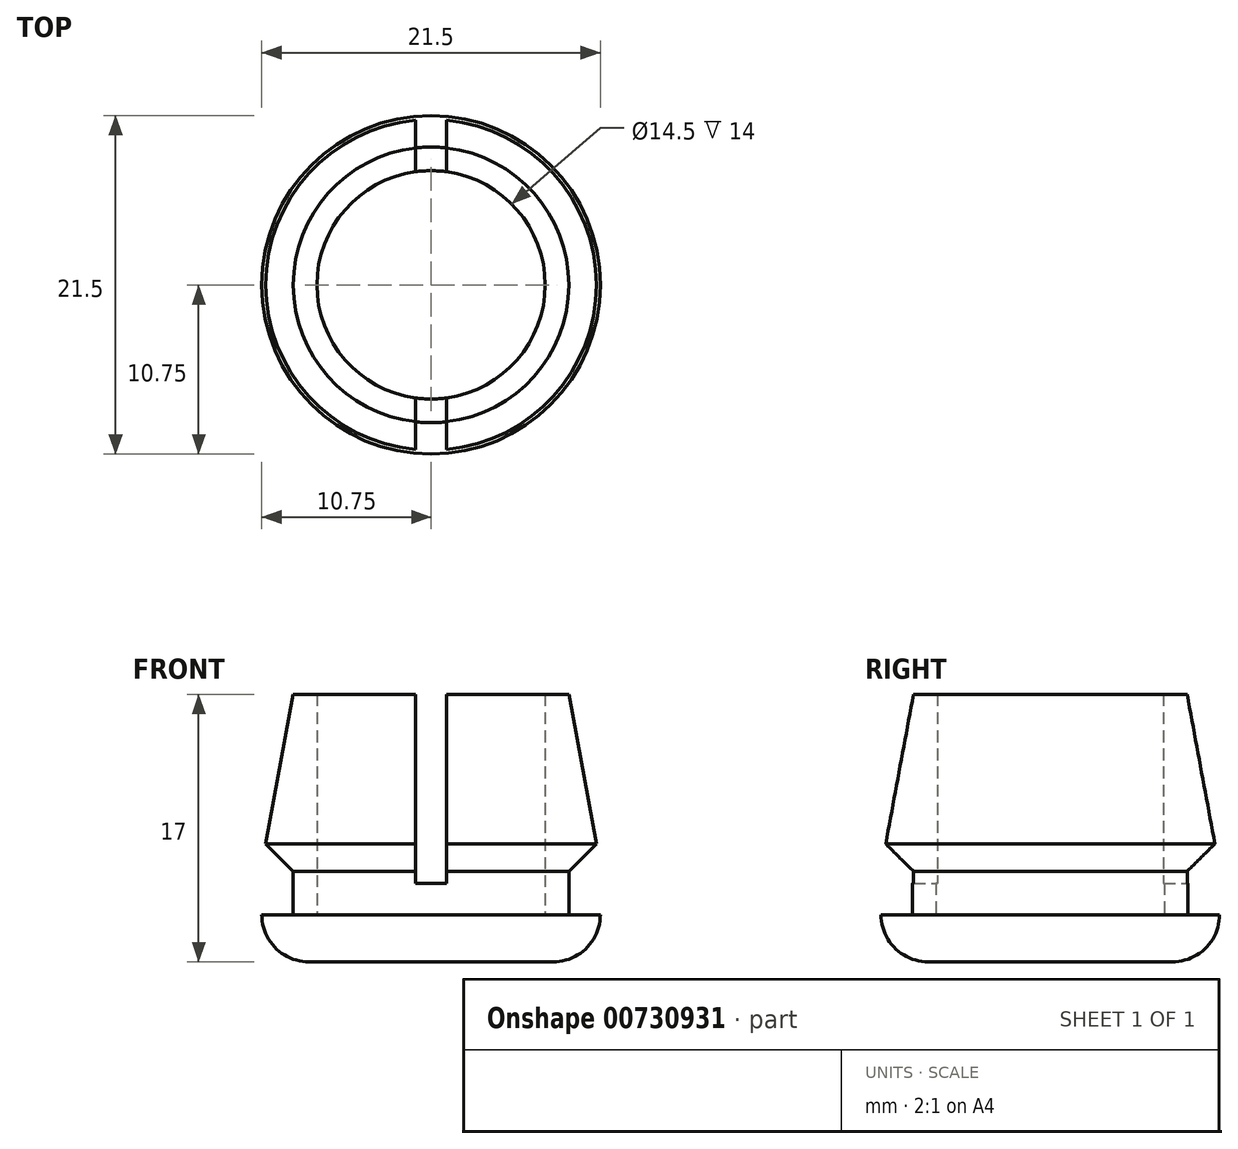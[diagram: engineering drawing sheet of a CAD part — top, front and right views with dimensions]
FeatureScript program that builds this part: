
annotation { "Feature Type Name" : "Feature", "Feature Type Description" : "" }
export const myFeature = defineFeature(function(context is Context, id is Id, definition is map)
    precondition{}
    {
        {
            var Q0;
            Q0=qCreatedBy(makeId("Front.planeOp"),FACE);
            var sketch = newSketch(context, id + "F0", { "sketchPlane" : qUnion([Q0])});
            skLineSegment(sketch, "E0", {"start": v(0, 0) * mm, "end": v(10.75, 0) * mm});
            skLineSegment(sketch, "E1", {"start": v(10.75, 0) * mm, "end": v(10.75, 3) * mm});
            skLineSegment(sketch, "E2", {"start": v(10.75, 3) * mm, "end": v(8.75, 3) * mm});
            skLineSegment(sketch, "E3", {"start": v(8.75, 3) * mm, "end": v(8.75, 7.5) * mm});
            skLineSegment(sketch, "E4", {"start": v(8.75, 7.5) * mm, "end": v(10.5, 7.5) * mm});
            skLineSegment(sketch, "E5", {"start": v(10.5, 7.5) * mm, "end": v(8.75, 17) * mm});
            skLineSegment(sketch, "E6", {"start": v(8.75, 17) * mm, "end": v(7.25, 17) * mm});
            skLineSegment(sketch, "E7", {"start": v(7.25, 17) * mm, "end": v(7.25, 3) * mm});
            skLineSegment(sketch, "E8", {"start": v(7.25, 3) * mm, "end": v(0, 3) * mm});
            skLineSegment(sketch, "E9", {"start": v(0, 0) * mm, "end": v(0, 3) * mm});
            skSolve(sketch);
        }
        {
            var Q0;
            Q0=makeQuery(id+"F0.imprint","IMPRINT",FACE,{"disambiguationData":[TD([[makeQuery(id+"F0.imprint","IMPRINT",EDGE,{"derivedFrom":sQuery(id+"F0.wireOp",EDGE,"E0")}),1.0]])]});
            var Q1;
            Q1 = qConstructionFilter(qBodyType(qCreatedBy(id + "F0" ,EDGE), BodyType.WIRE), ConstructionObject.NO);
            var Q2;
            Q2=sQuery(id+"F0.wireOp",EDGE,"E9");
            revolve(context, id + "F1", {"surfaceOperationType" : NewSurfaceOperationType.NEW, "entities" : qUnion([Q0]), "surfaceEntities" : qUnion([Q1]), "axis" : qUnion([Q2]), "revolveType" : RevolveType.FULL});
        }
        {
            var Q0;
            Q0=makeQuery(id+"F1.opRevolve","SWEPT_FACE",FACE,{"disambiguationData":[OSD([sQuery(id+"F0.wireOp",EDGE,"E6")])]});
            var sketch = newSketch(context, id + "F2", { "sketchPlane" : qUnion([Q0])});
            skLineSegment(sketch, "E10.bottom", {"start": v(1, 25) * mm, "end": v(-1, 25) * mm});
            skLineSegment(sketch, "E10.top", {"start": v(1, -25) * mm, "end": v(-1, -25) * mm});
            skLineSegment(sketch, "E10.left", {"start": v(1, 25) * mm, "end": v(1, -25) * mm});
            skLineSegment(sketch, "E10.right", {"start": v(-1, 25) * mm, "end": v(-1, -25) * mm});
            skPoint(sketch, "E10.middle", {"position": v(0, 0) * mm});
            skSolve(sketch);
        }
        {
            var Q0;
            {var subQ0=sQuery(id+"F2.wireOp",EDGE,"E10.left");var subQ1=makeQuery(id+"F1.opRevolve","SWEPT_EDGE",EDGE,{"disambiguationData":[OSD([sQuery(id+"F0.wireOp",EDGE,"E6"),sQuery(id+"F0.wireOp",EDGE,"E7")])]});var subQ2=makeQuery(id+"F2.imprint","INTERSECT",VERTEX,{"disambiguationData":[OD(0.0)],"derivedFrom":[subQ1,subQ0]});Q0=makeQuery(id+"F2.imprint","IMPRINT",FACE,{"disambiguationData":[TD([[makeQuery(id+"F2.imprint","IMPRINT",EDGE,{"disambiguationData":[TD([[subQ2,-1.0]])],"derivedFrom":subQ0}),-1.0]])]});}
            var Q1;
            {var subQ0=sQuery(id+"F2.wireOp",EDGE,"E10.left");var subQ1=sQuery(id+"F0.wireOp",EDGE,"E6");var subQ2=makeQuery(id+"F1.opRevolve","SWEPT_EDGE",EDGE,{"disambiguationData":[OSD([sQuery(id+"F0.wireOp",EDGE,"E5"),subQ1])]});var subQ3=makeQuery(id+"F2.imprint","INTERSECT",VERTEX,{"disambiguationData":[OD(0.0)],"derivedFrom":[subQ2,subQ0]});Q1=makeQuery(id+"F2.imprint","IMPRINT",FACE,{"disambiguationData":[TD([[makeQuery(id+"F2.imprint","IMPRINT",EDGE,{"disambiguationData":[TD([[subQ3,-1.0]])],"derivedFrom":subQ0}),-1.0]])]});}
            var Q2;
            {var subQ0=sQuery(id+"F2.wireOp",EDGE,"E10.left");var subQ1=sQuery(id+"F0.wireOp",EDGE,"E6");var subQ2=makeQuery(id+"F1.opRevolve","SWEPT_EDGE",EDGE,{"disambiguationData":[OSD([sQuery(id+"F0.wireOp",EDGE,"E5"),subQ1])]});var subQ3=makeQuery(id+"F2.imprint","INTERSECT",VERTEX,{"disambiguationData":[OD(1.0)],"derivedFrom":[subQ2,subQ0]});Q2=makeQuery(id+"F2.imprint","IMPRINT",FACE,{"disambiguationData":[TD([[makeQuery(id+"F2.imprint","IMPRINT",EDGE,{"disambiguationData":[TD([[subQ3,1.0]])],"derivedFrom":subQ0}),-1.0]])]});}
            var Q3;
            {var subQ0=sQuery(id+"F2.wireOp",EDGE,"E10.top");Q3=makeQuery(id+"F2.imprint","IMPRINT",FACE,{"disambiguationData":[TD([[makeQuery(id+"F2.imprint","IMPRINT",EDGE,{"derivedFrom":subQ0}),-1.0]])]});}
            var Q4;
            {var subQ0=sQuery(id+"F2.wireOp",EDGE,"E10.bottom");Q4=makeQuery(id+"F2.imprint","IMPRINT",FACE,{"disambiguationData":[TD([[makeQuery(id+"F2.imprint","IMPRINT",EDGE,{"derivedFrom":subQ0}),1.0]])]});}
            var Q5;
            Q5=makeQuery(id+"F1.opRevolve","SWEPT_FACE",FACE,{"disambiguationData":[OSD([sQuery(id+"F0.wireOp",EDGE,"E2")])]});
            extrude(context, id + "F3", {"entities" : qUnion([Q0, Q1, Q2, Q3, Q4]), "operationType" : NewBodyOperationType.REMOVE, "endBound" : BoundingType.UP_TO_SURFACE, "oppositeDirection" : true, "depth" : 13.2 * mm, "endBoundEntityFace" : qUnion([Q5]), "hasOffset" : true, "offsetDistance" : 2 * mm});
        }
        {
            var Q0;
            Q0=makeQuery(id+"F1.opRevolve","SWEPT_EDGE",EDGE,{"disambiguationData":[OSD([sQuery(id+"F0.wireOp",EDGE,"E0"),sQuery(id+"F0.wireOp",EDGE,"E1")])]});
            fillet(context, id + "F4", {"entities" : qUnion([Q0]), "radius" : 3 * mm, "tangentPropagation" : true, "allowEdgeOverflow" : false});
        }
        {
            var Q0;
            {var subQ0=sQuery(id+"F0.wireOp",EDGE,"E3");var subQ1=sQuery(id+"F0.wireOp",EDGE,"E4");Q0=makeQuery(id+"F3.boolean.opBoolean","SPLIT",EDGE,{"disambiguationData":[TD([makeQuery(id+"F3.opExtrude","SWEPT_FACE",FACE,{"disambiguationData":[OSD([sQuery(id+"F2.wireOp",EDGE,"E10.right")])]})])],"derivedFrom":makeQuery(id+"F1.opRevolve","SWEPT_EDGE",EDGE,{"disambiguationData":[OSD([subQ0,subQ1])]})});}
            var Q1;
            {var subQ0=sQuery(id+"F0.wireOp",EDGE,"E3");var subQ1=sQuery(id+"F0.wireOp",EDGE,"E4");Q1=makeQuery(id+"F3.boolean.opBoolean","SPLIT",EDGE,{"disambiguationData":[TD([makeQuery(id+"F3.opExtrude","SWEPT_FACE",FACE,{"disambiguationData":[OSD([sQuery(id+"F2.wireOp",EDGE,"E10.left")])]})])],"derivedFrom":makeQuery(id+"F1.opRevolve","SWEPT_EDGE",EDGE,{"disambiguationData":[OSD([subQ0,subQ1])]})});}
            chamfer(context, id + "F5", {"entities" : qUnion([Q0, Q1]), "width" : 1.75 * mm, "tangentPropagation" : true});
        }
    });
